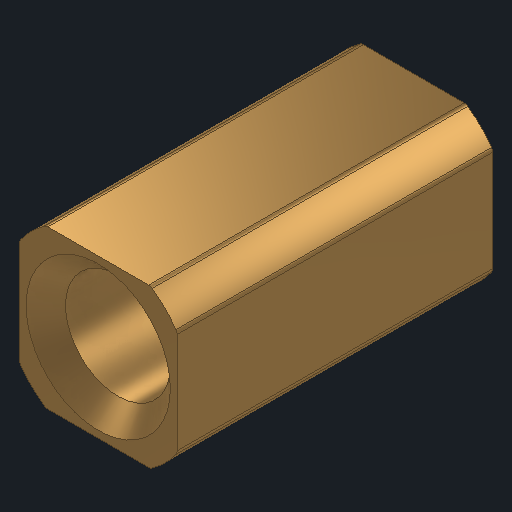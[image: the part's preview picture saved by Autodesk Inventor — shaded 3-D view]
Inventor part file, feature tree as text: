
AUTODESK INVENTOR PART (.ipt)
format: ipt  version: 2024 (Build 280153000, 153)  size: 164,352 bytes
history: native  units: in
note: dims shown in document units (in); Inventor stores cm internally (conversion verified against a paired STEP export)
features: other x3, sketch x2
ambient origin geometry x8: Origin, YZ Plane, XZ Plane, XY Plane, X Axis, Y Axis, Z Axis, Center Point
bodies: Solid1 (feature_tree)
feature tree (5):
  other  "HS Shaft Adapter Circle.ipt"
  other  "Solid1::HS Shaft Adapter Circle.ipt"
  other  "TaggingFeature1"
  sketch  "Sketch1"  dims[d0=0.3937in]
  sketch  "Sketch2"
